# Revit family: Lighting_Fixture-Wall-Astro-Zip
name_source: partatom
category: Lighting Fixtures
revit_build: Autodesk Revit LT 2016 (Build: 20150220_1215(x64)
units: mm (PartAtom-declared; Revit-internal decimal feet)

## family parameters
Cut with Voids When Loaded = No
Host = Face
Light Source = No
OmniClass Number = 23.80.70.00
OmniClass Title = Lighting
Part Type = Normal
Room Calculation Point = No
Round Connector Dimension = Use Diameter
Shared = No

## types (1)
- Type 1
    Apparent Load = 4 VA
    Assembly Code = D5020200
    Casing Material = Astro - Steel - Chrome Finish
    Class = 2
    Description = Mirror Light
    Dimmable = No
    Energy Efficiency Rating = A
    Height = 40 mm  [stored 0.131234 ft]
    IP Rating = IP44
    Lamp = LED
    Lamp included = Yes
    Length = 230 mm  [stored 0.754593 ft]
    Light Source Elevation = 1610 mm  [stored 5.28215 ft]
    Light Source From Wall = 207 mm  [stored 0.679134 ft]
    Luminaire Lamp Efficiency Rating = A
    Manufacturer = Astro Lighting Ltd, CM20 2DP
    Model = 7009 Zip
    Mountable on normally flammable surfaces = Yes
    Number of Poles = 1
    Product Documentation = http://www.astrolighting.co.uk
/kw/7009/7009_Zip
    Suitable for bathroom zone = zone 2, 3
    Type Comments = - Includes integral electronic LED driver
    URL = www.astrolighting.co.uk
    Voltage = 230 V
    Wattage Comments = 3x1
    Weight = 1.0 kg
    Width = 300 mm

note: [stored X ft] marks values corroborated as IEEE doubles in the binary element streams (Revit-internal decimal feet)

## geometry (parser evidence)
native form markers: Sweep x6
no freeform markers — native parametric forms only
